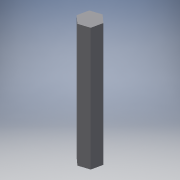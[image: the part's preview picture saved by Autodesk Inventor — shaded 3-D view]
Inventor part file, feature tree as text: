
AUTODESK INVENTOR PART (.ipt)
format: ipt  version: 2018 (Build 220112000, 112)  size: 95,232 bytes
history: native  units: in
note: dims shown in document units (in); Inventor stores cm internally (conversion verified against a paired STEP export)
features: extrude x1, sketch x1
ambient origin geometry x8: Origin, YZ Plane, XZ Plane, XY Plane, X Axis, Y Axis, Z Axis, Center Point
bodies: Solid1 (feature_tree)
feature tree (2):
  extrude  "Extrusion1"  Depth=2.5in TaperAngle=0.0deg
  sketch  "Sketch1"  dims[d0=0.375in d1=2.5in d2=0.0in]
